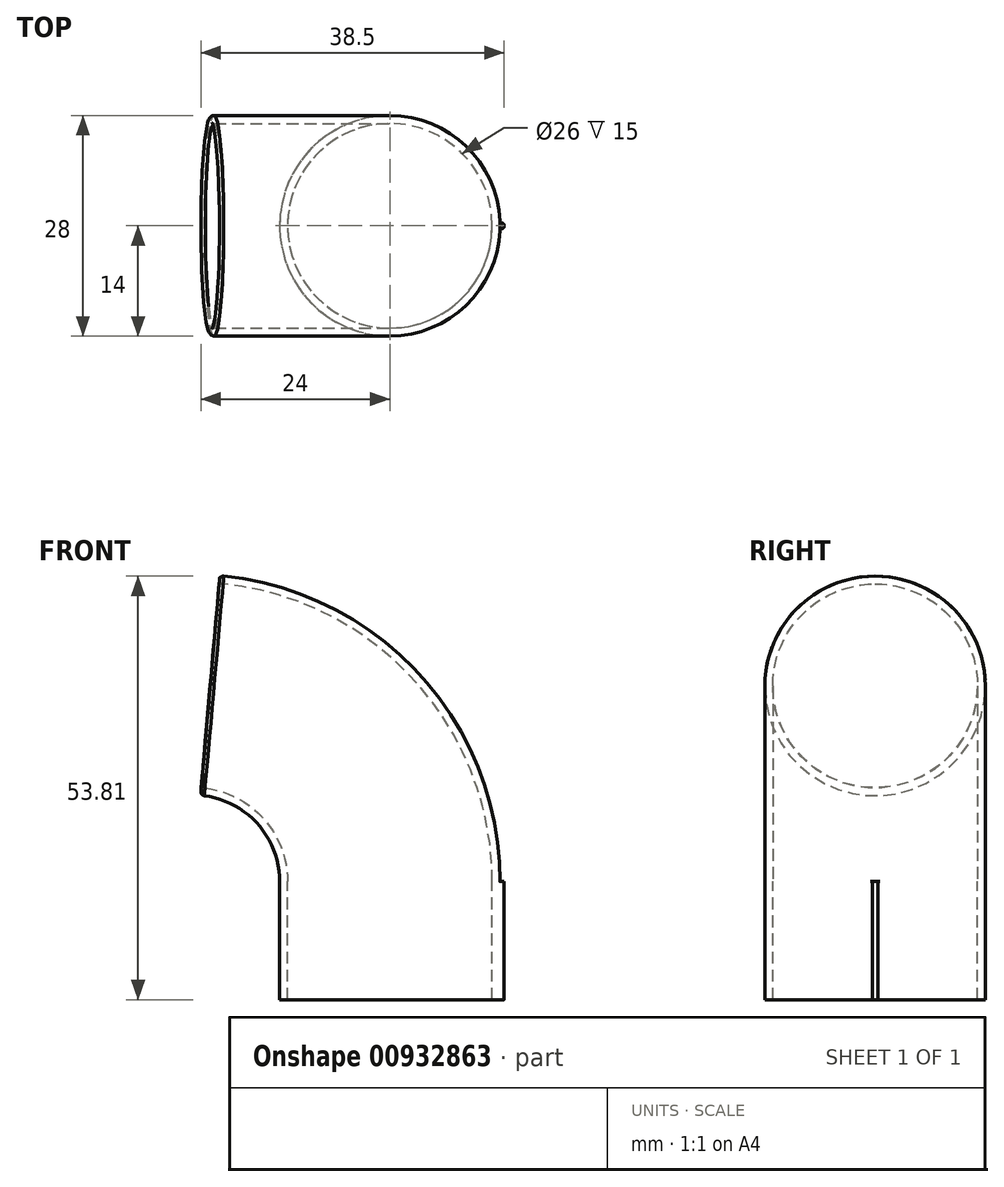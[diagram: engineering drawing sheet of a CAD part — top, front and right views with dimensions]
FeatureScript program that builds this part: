
annotation { "Feature Type Name" : "Feature", "Feature Type Description" : "" }
export const myFeature = defineFeature(function(context is Context, id is Id, definition is map)
    precondition{}
    {
        {
            var Q0;
            Q0=qCreatedBy(makeId("Top.planeOp"),FACE);
            var sketch = newSketch(context, id + "F0", { "sketchPlane" : qUnion([Q0])});
            skCircle(sketch, "E0", {"center": v(0, 0) * mm, "radius": 14 * mm});
            skCircle(sketch, "E1", {"center": v(0, 0) * mm, "radius": 13 * mm});
            skSolve(sketch);
        }
        {
            var Q0;
            Q0=qCreatedBy(makeId("Front.planeOp"),FACE);
            var sketch = newSketch(context, id + "F1", { "sketchPlane" : qUnion([Q0])});
            skLineSegment(sketch, "E2", {"start": v(0, 0) * mm, "end": v(0, 15) * mm});
            skArc(sketch, "E3", {"start": v(0, 15) * mm, "mid": v(-6.57, 31.89) * mm, "end": v(-22.82, 39.9) * mm});
            skLineSegment(sketch, "E4", {"start": v(0, 15) * mm, "end": v(-25, 15) * mm, "construction": true});
            skLineSegment(sketch, "E5", {"start": v(-22.82, 39.9) * mm, "end": v(-25, 15) * mm, "construction": true});
            skSolve(sketch);
        }
        {
            var Q0;
            Q0=makeQuery(id+"F0.imprint","IMPRINT",FACE,{"disambiguationData":[TD([[makeQuery(id+"F0.imprint","IMPRINT",EDGE,{"derivedFrom":sQuery(id+"F0.wireOp",EDGE,"E0")}),1.0]])]});
            var Q1;
            Q1=sQuery(id+"F1.wireOp",EDGE,"E2");
            var Q2;
            Q2=sQuery(id+"F1.wireOp",EDGE,"E3");
            sweep(context, id + "F2", {"profiles" : qUnion([Q0]), "path" : qUnion([Q1, Q2])});
        }
        {
            var Q0;
            Q0=qCreatedBy(makeId("Top.planeOp"),FACE);
            var sketch = newSketch(context, id + "F3", { "sketchPlane" : qUnion([Q0])});
            skLineSegment(sketch, "E6.bottom", {"start": v(14.5, -0.35) * mm, "end": v(13.5, -0.35) * mm});
            skLineSegment(sketch, "E6.top", {"start": v(14.5, 0.35) * mm, "end": v(13.5, 0.35) * mm});
            skLineSegment(sketch, "E6.left", {"start": v(14.5, -0.35) * mm, "end": v(14.5, 0.35) * mm});
            skLineSegment(sketch, "E6.right", {"start": v(13.5, -0.35) * mm, "end": v(13.5, 0.35) * mm});
            skPoint(sketch, "E6.middle", {"position": v(14, 0) * mm});
            skSolve(sketch);
        }
        {
            var Q0;
            Q0 = qSketchRegion(id + "F3", true);
            extrude(context, id + "F4", {"entities" : qUnion([Q0]), "operationType" : NewBodyOperationType.ADD, "depth" : 15 * mm, "offsetDistance" : 25 * mm});
        }
        {
            var Q0;
            Q0=makeQuery(id+"F4.opExtrude","SWEPT_EDGE",EDGE,{"disambiguationData":[OSD([sQuery(id+"F3.wireOp",EDGE,"E6.top"),sQuery(id+"F3.wireOp",EDGE,"E6.left")])]});
            var Q1;
            Q1=makeQuery(id+"F4.boolean.opBoolean","INTERSECT",EDGE,{"derivedFrom":[makeQuery(id+"F2.opSweep","SWEPT_FACE",FACE,{"disambiguationData":[OSD([sQuery(id+"F0.wireOp",EDGE,"E0"),sQuery(id+"F1.wireOp",EDGE,"E2")])]}),makeQuery(id+"F4.opExtrude","SWEPT_FACE",FACE,{"disambiguationData":[OSD([sQuery(id+"F3.wireOp",EDGE,"E6.top")])]})]});
            var Q2;
            Q2=makeQuery(id+"F4.opExtrude","SWEPT_EDGE",EDGE,{"disambiguationData":[OSD([sQuery(id+"F3.wireOp",EDGE,"E6.bottom"),sQuery(id+"F3.wireOp",EDGE,"E6.left")])]});
            var Q3;
            Q3=makeQuery(id+"F4.boolean.opBoolean","INTERSECT",EDGE,{"derivedFrom":[makeQuery(id+"F2.opSweep","SWEPT_FACE",FACE,{"disambiguationData":[OSD([sQuery(id+"F0.wireOp",EDGE,"E0"),sQuery(id+"F1.wireOp",EDGE,"E2")])]}),makeQuery(id+"F4.opExtrude","SWEPT_FACE",FACE,{"disambiguationData":[OSD([sQuery(id+"F3.wireOp",EDGE,"E6.bottom")])]})]});
            fillet(context, id + "F5", {"entities" : qUnion([Q0, Q1, Q2, Q3]), "radius" : .25 * mm, "tangentPropagation" : true, "allowEdgeOverflow" : false});
        }
        {
            var Q0;
            Q0=makeQuery(id+"F2.opSweep","CAP_EDGE",EDGE,{"disambiguationData":[OSD([sQuery(id+"F0.wireOp",EDGE,"E1"),sQuery(id+"F1.wireOp",VERTEX,"E3.end")])],"isStart":false});
            var Q1;
            Q1=makeQuery(id+"F2.opSweep","CAP_EDGE",EDGE,{"disambiguationData":[OSD([sQuery(id+"F0.wireOp",EDGE,"E0"),sQuery(id+"F1.wireOp",VERTEX,"E3.end")])],"isStart":false});
            fillet(context, id + "F6", {"entities" : qUnion([Q0, Q1]), "radius" : .5 * mm, "tangentPropagation" : true, "allowEdgeOverflow" : false});
        }
    });
